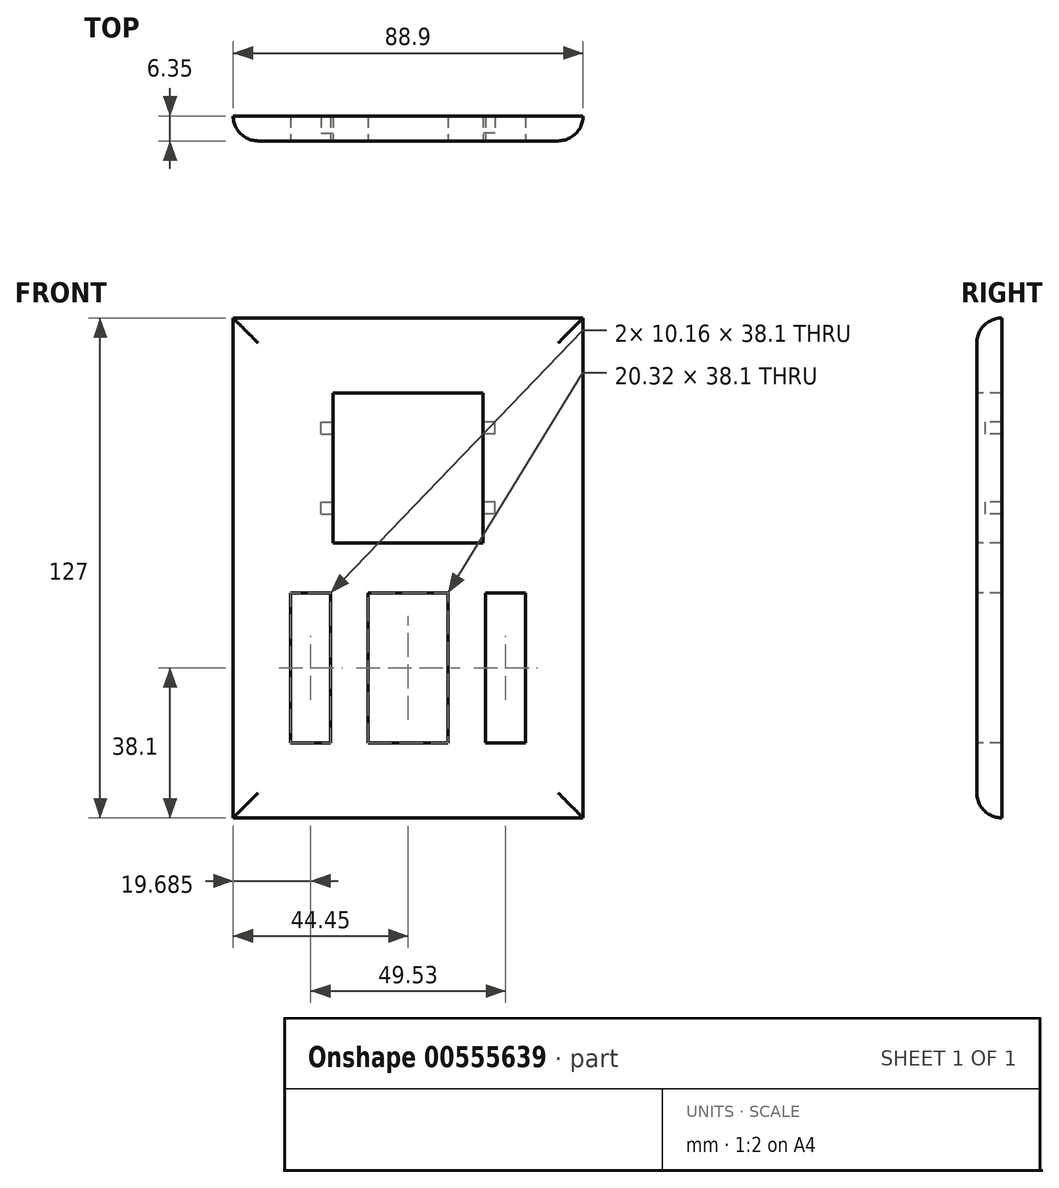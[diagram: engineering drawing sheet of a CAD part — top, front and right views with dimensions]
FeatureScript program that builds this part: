
annotation { "Feature Type Name" : "Feature", "Feature Type Description" : "" }
export const myFeature = defineFeature(function(context is Context, id is Id, definition is map)
    precondition{}
    {
        {
            var Q0;
            Q0=qCreatedBy(makeId("Front.planeOp"),FACE);
            var sketch = newSketch(context, id + "F0", { "sketchPlane" : qUnion([Q0])});
            skLineSegment(sketch, "E0.bottom", {"start": v(44.45, -63.5) * mm, "end": v(-44.45, -63.5) * mm});
            skLineSegment(sketch, "E0.top", {"start": v(44.45, 63.5) * mm, "end": v(-44.45, 63.5) * mm});
            skLineSegment(sketch, "E0.left", {"start": v(44.45, -63.5) * mm, "end": v(44.45, 63.5) * mm});
            skLineSegment(sketch, "E0.right", {"start": v(-44.45, -63.5) * mm, "end": v(-44.45, 63.5) * mm});
            skPoint(sketch, "E0.middle", {"position": v(0, 0) * mm});
            skSolve(sketch);
        }
        {
            var Q0;
            Q0=makeQuery(id+"F0.imprint","IMPRINT",FACE,{"disambiguationData":[TD([[makeQuery(id+"F0.imprint","IMPRINT",EDGE,{"derivedFrom":sQuery(id+"F0.wireOp",EDGE,"E0.bottom")}),-1.0]])]});
            extrude(context, id + "F1", {"entities" : qUnion([Q0]), "depth" : 6.35 * mm, "offsetDistance" : 25.4 * mm});
        }
        {
            var Q0;
            Q0=makeQuery(id+"F1.opExtrude","CAP_EDGE",EDGE,{"disambiguationData":[OSD([sQuery(id+"F0.wireOp",EDGE,"E0.right")])],"isStart":false});
            var Q1;
            Q1=makeQuery(id+"F1.opExtrude","CAP_EDGE",EDGE,{"disambiguationData":[OSD([sQuery(id+"F0.wireOp",EDGE,"E0.top")])],"isStart":false});
            var Q2;
            Q2=makeQuery(id+"F1.opExtrude","CAP_EDGE",EDGE,{"disambiguationData":[OSD([sQuery(id+"F0.wireOp",EDGE,"E0.left")])],"isStart":false});
            var Q3;
            Q3=makeQuery(id+"F1.opExtrude","CAP_EDGE",EDGE,{"disambiguationData":[OSD([sQuery(id+"F0.wireOp",EDGE,"E0.bottom")])],"isStart":false});
            fillet(context, id + "F2", {"entities" : qUnion([Q0, Q1, Q2, Q3]), "radius" : 6.35 * mm, "tangentPropagation" : true, "allowEdgeOverflow" : false});
        }
        {
            var Q0;
            Q0=makeQuery(id+"F1.opExtrude","CAP_FACE",FACE,{"disambiguationData":[OSD([sQuery(id+"F0.wireOp",EDGE,"E0.bottom"),sQuery(id+"F0.wireOp",EDGE,"E0.top"),sQuery(id+"F0.wireOp",EDGE,"E0.left"),sQuery(id+"F0.wireOp",EDGE,"E0.right")])],"isStart":false});
            var sketch = newSketch(context, id + "F3", { "sketchPlane" : qUnion([Q0])});
            skLineSegment(sketch, "E1.bottom", {"start": v(19.05, 6.35) * mm, "end": v(-19.05, 6.35) * mm});
            skLineSegment(sketch, "E1.top", {"start": v(19.05, 44.45) * mm, "end": v(-19.05, 44.45) * mm});
            skLineSegment(sketch, "E1.left", {"start": v(19.05, 6.35) * mm, "end": v(19.05, 44.45) * mm});
            skLineSegment(sketch, "E1.right", {"start": v(-19.05, 6.35) * mm, "end": v(-19.05, 44.45) * mm});
            skPoint(sketch, "E1.middle", {"position": v(0, 25.4) * mm});
            skSolve(sketch);
        }
        {
            var Q0;
            Q0=makeQuery(id+"F3.imprint","IMPRINT",FACE,{"disambiguationData":[TD([[makeQuery(id+"F3.imprint","IMPRINT",EDGE,{"derivedFrom":sQuery(id+"F3.wireOp",EDGE,"E1.bottom")}),-1.0]])]});
            extrude(context, id + "F4", {"entities" : qUnion([Q0]), "operationType" : NewBodyOperationType.REMOVE, "endBound" : BoundingType.THROUGH_ALL, "oppositeDirection" : true, "depth" : 25.4 * mm, "offsetDistance" : 25.4 * mm});
        }
        {
            var Q0;
            Q0=makeQuery(id+"F1.opExtrude","CAP_FACE",FACE,{"disambiguationData":[OSD([sQuery(id+"F0.wireOp",EDGE,"E0.bottom"),sQuery(id+"F0.wireOp",EDGE,"E0.top"),sQuery(id+"F0.wireOp",EDGE,"E0.left"),sQuery(id+"F0.wireOp",EDGE,"E0.right")])],"isStart":false});
            var sketch = newSketch(context, id + "F5", { "sketchPlane" : qUnion([Q0])});
            skLineSegment(sketch, "E2.bottom", {"start": v(10.16, -44.45) * mm, "end": v(-10.16, -44.45) * mm});
            skLineSegment(sketch, "E2.top", {"start": v(10.16, -6.35) * mm, "end": v(-10.16, -6.35) * mm});
            skLineSegment(sketch, "E2.left", {"start": v(10.16, -44.45) * mm, "end": v(10.16, -6.35) * mm});
            skLineSegment(sketch, "E2.right", {"start": v(-10.16, -44.45) * mm, "end": v(-10.16, -6.35) * mm});
            skPoint(sketch, "E2.middle", {"position": v(0, -25.4) * mm});
            skLineSegment(sketch, "E3.bottom", {"start": v(-19.68, -44.45) * mm, "end": v(-29.85, -44.45) * mm});
            skLineSegment(sketch, "E3.top", {"start": v(-19.69, -6.35) * mm, "end": v(-29.85, -6.35) * mm});
            skLineSegment(sketch, "E3.left", {"start": v(-19.68, -44.45) * mm, "end": v(-19.69, -6.35) * mm});
            skLineSegment(sketch, "E3.right", {"start": v(-29.85, -44.45) * mm, "end": v(-29.85, -6.35) * mm});
            skPoint(sketch, "E3.middle", {"position": v(-24.77, -25.4) * mm});
            skLineSegment(sketch, "E4.bottom", {"start": v(29.85, -44.45) * mm, "end": v(19.69, -44.45) * mm});
            skLineSegment(sketch, "E4.top", {"start": v(29.85, -6.35) * mm, "end": v(19.69, -6.35) * mm});
            skLineSegment(sketch, "E4.left", {"start": v(29.85, -44.45) * mm, "end": v(29.85, -6.35) * mm});
            skLineSegment(sketch, "E4.right", {"start": v(19.69, -44.45) * mm, "end": v(19.69, -6.35) * mm});
            skPoint(sketch, "E4.middle", {"position": v(24.77, -25.4) * mm});
            skSolve(sketch);
        }
        {
            var Q0;
            Q0=makeQuery(id+"F5.imprint","IMPRINT",FACE,{"disambiguationData":[TD([[makeQuery(id+"F5.imprint","IMPRINT",EDGE,{"derivedFrom":sQuery(id+"F5.wireOp",EDGE,"E2.bottom")}),-1.0]])]});
            var Q1;
            Q1=makeQuery(id+"F5.imprint","IMPRINT",FACE,{"disambiguationData":[TD([[makeQuery(id+"F5.imprint","IMPRINT",EDGE,{"derivedFrom":sQuery(id+"F5.wireOp",EDGE,"E3.bottom")}),-1.0]])]});
            var Q2;
            Q2=makeQuery(id+"F5.imprint","IMPRINT",FACE,{"disambiguationData":[TD([[makeQuery(id+"F5.imprint","IMPRINT",EDGE,{"derivedFrom":sQuery(id+"F5.wireOp",EDGE,"E4.bottom")}),-1.0]])]});
            extrude(context, id + "F6", {"entities" : qUnion([Q0, Q1, Q2]), "operationType" : NewBodyOperationType.REMOVE, "endBound" : BoundingType.THROUGH_ALL, "oppositeDirection" : true, "depth" : 25.4 * mm, "offsetDistance" : 25.4 * mm});
        }
        {
            var Q0;
            Q0=makeQuery(id+"F4.boolean.opBoolean","COPY",FACE,{"derivedFrom":makeQuery(id+"F4.opExtrude","SWEPT_FACE",FACE,{"disambiguationData":[OSD([sQuery(id+"F3.wireOp",EDGE,"E1.right")])]})});
            var sketch = newSketch(context, id + "F7", { "sketchPlane" : qUnion([Q0])});
            skLineSegment(sketch, "E5.bottom", {"start": v(0, 37.08) * mm, "end": v(-4.32, 37.08) * mm});
            skLineSegment(sketch, "E5.top", {"start": v(0, 34.04) * mm, "end": v(-4.32, 34.04) * mm});
            skLineSegment(sketch, "E5.left", {"start": v(0, 37.08) * mm, "end": v(0, 34.04) * mm});
            skLineSegment(sketch, "E5.right", {"start": v(-4.32, 37.08) * mm, "end": v(-4.32, 34.04) * mm});
            skLineSegment(sketch, "E6.bottom", {"start": v(0, 16.76) * mm, "end": v(-4.32, 16.76) * mm});
            skLineSegment(sketch, "E6.top", {"start": v(0, 13.72) * mm, "end": v(-4.32, 13.72) * mm});
            skLineSegment(sketch, "E6.left", {"start": v(0, 16.76) * mm, "end": v(0, 13.72) * mm});
            skLineSegment(sketch, "E6.right", {"start": v(-4.32, 16.76) * mm, "end": v(-4.32, 13.72) * mm});
            skSolve(sketch);
        }
        {
            var Q0;
            Q0 = qSketchRegion(id + "F7", true);
            extrude(context, id + "F8", {"entities" : qUnion([Q0]), "operationType" : NewBodyOperationType.REMOVE, "oppositeDirection" : true, "depth" : 3.05 * mm, "offsetDistance" : 25.4 * mm});
        }
        {
            var Q0;
            Q0=makeQuery(id+"F4.boolean.opBoolean","COPY",FACE,{"derivedFrom":makeQuery(id+"F4.opExtrude","SWEPT_FACE",FACE,{"disambiguationData":[OSD([sQuery(id+"F3.wireOp",EDGE,"E1.left")])]})});
            var sketch = newSketch(context, id + "F9", { "sketchPlane" : qUnion([Q0])});
            skLineSegment(sketch, "E7.bottom", {"start": v(0, 16.76) * mm, "end": v(4.32, 16.76) * mm});
            skLineSegment(sketch, "E7.top", {"start": v(0, 13.72) * mm, "end": v(4.32, 13.72) * mm});
            skLineSegment(sketch, "E7.left", {"start": v(0, 16.76) * mm, "end": v(0, 13.72) * mm});
            skLineSegment(sketch, "E7.right", {"start": v(4.32, 16.76) * mm, "end": v(4.32, 13.72) * mm});
            skLineSegment(sketch, "E8.bottom", {"start": v(0, 37.08) * mm, "end": v(4.32, 37.08) * mm});
            skLineSegment(sketch, "E8.top", {"start": v(0, 34.04) * mm, "end": v(4.32, 34.04) * mm});
            skLineSegment(sketch, "E8.left", {"start": v(0, 37.08) * mm, "end": v(0, 34.04) * mm});
            skLineSegment(sketch, "E8.right", {"start": v(4.32, 37.08) * mm, "end": v(4.32, 34.04) * mm});
            skSolve(sketch);
        }
        {
            var Q0;
            Q0 = qSketchRegion(id + "F9", true);
            extrude(context, id + "F10", {"entities" : qUnion([Q0]), "operationType" : NewBodyOperationType.REMOVE, "oppositeDirection" : true, "depth" : 3.05 * mm, "offsetDistance" : 25.4 * mm});
        }
    });
